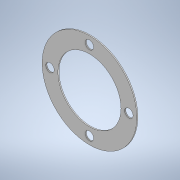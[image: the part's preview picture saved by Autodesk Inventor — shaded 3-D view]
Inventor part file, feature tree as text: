
AUTODESK INVENTOR PART (.ipt)
format: ipt  version: 2021 (Build 250183000, 183)  size: 117,248 bytes
history: native  units: mm
features: extrude x1, sketch x1
ambient origin geometry x8: Origin, YZ Plane, XZ Plane, XY Plane, X Axis, Y Axis, Z Axis, Center Point
bodies: Solid1 (feature_tree)
feature tree (2):
  extrude  "Extrusion1"  Depth=1.0mm
  sketch  "Sketch1"  dims[d0=90.0mm d1=60.0mm d2=8.0mm d3=37.5mm d4=40.0mm d6=360.0deg d8=75.0mm d9=37.5mm d10=37.5mm d11=75.0mm d12=1.0mm d13=0.0mm]
